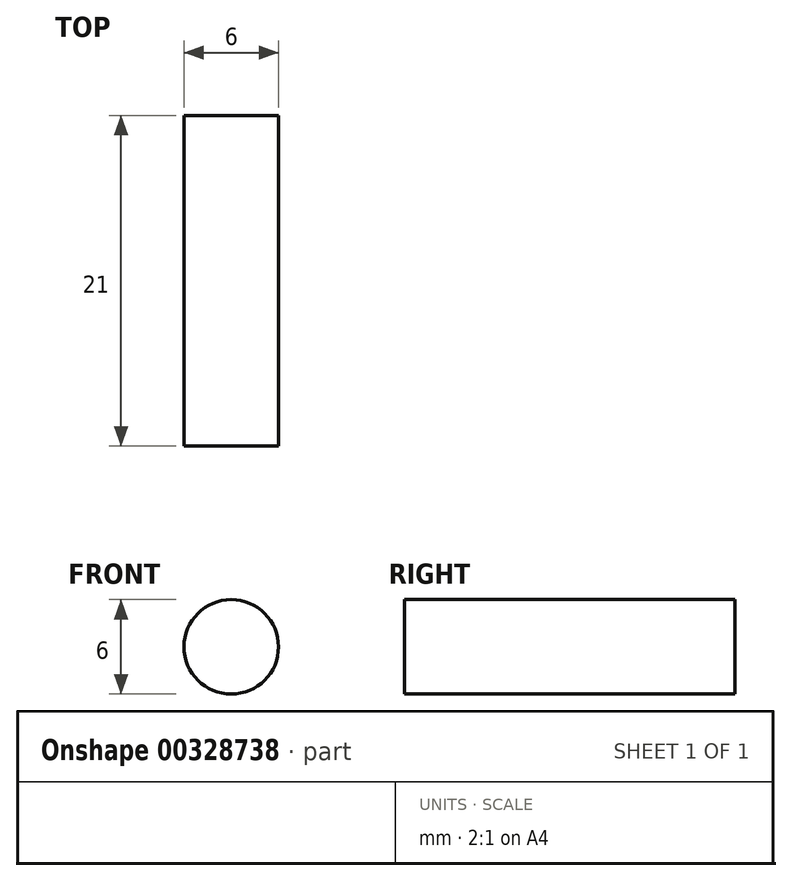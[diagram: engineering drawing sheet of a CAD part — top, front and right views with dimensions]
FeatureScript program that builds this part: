
annotation { "Feature Type Name" : "Feature", "Feature Type Description" : "" }
export const myFeature = defineFeature(function(context is Context, id is Id, definition is map)
    precondition{}
    {
        {
            var Q0;
            Q0=qCreatedBy(makeId("Front.planeOp"),FACE);
            var sketch = newSketch(context, id + "F0", { "sketchPlane" : qUnion([Q0])});
            skCircle(sketch, "E0", {"center": v(0, 0) * mm, "radius": 3 * mm});
            skSolve(sketch);
        }
        {
            var Q0;
            Q0 = qSketchRegion(id + "F0", true);
            extrude(context, id + "F1", {"entities" : qUnion([Q0]), "depth" : 21 * mm});
        }
    });
